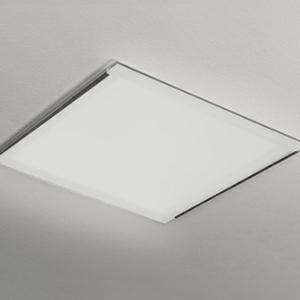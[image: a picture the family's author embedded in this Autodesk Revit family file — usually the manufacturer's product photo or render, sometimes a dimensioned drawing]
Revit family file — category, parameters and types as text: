
# Revit family: 3f_filippi_-_lucequadro_vop_3f_filippi_-_36584_-_lucequadro_led_3000_vop
name_source: partatom
category: Lighting Fixtures
units: mm (PartAtom-declared; Revit-internal decimal feet)

## family parameters
Cut with Voids When Loaded = No
Host = Face
Light Source = No
Part Type = Normal
Room Calculation Point = No
Round Connector Dimension = Use Diameter
Shared = No

## types (1)
- 3F Filippi - Lucequadro VOP (1 x LED, 1929 lm, 28 W, 4000 K)
    Apparent Load = 28 VA
    Approval mark = ENEC
    CIE Flux Codes = 47 79 96 100 100
    Color Rendering = 80
    Color Temperature = 4000 K
    Control Gear = Electronic ballast
    Default Elevation = 1800 mm
    Description = ILLUMINOTECHNICAL
Luminous efficiency 100% (DLOR 100%, ULOR 0%).
Initial luminous flux of the luminaire 1929 lm.
Direct distribution with soft, diffused and controlled light.
Installation Interdistance Transv.D = 1.25 x hu - Long.D = 1.24 x hu.
Tabular UGR (CIE 117 - 4H-8H; S=0.25H; 70/50/20): RUG 24.8 - 24.6.
Beam angle: 113° - 112°.
Luminous efficacy 69 lm/W.
Lifetime (L90/B10): 30000 h. (tq+25°C)
Lifetime (L85/B10): 50000 h. (tq+25°C)
Lifetime (L70/B10): 80000 h. (tq+25°C)
Sudden decreased luminous flux after 50000 hours: 0% (C0).
Photobiological safety in compliance with IEC/TR 62778: RG1 low risk, (IEC 62471).
In compliance with IEC/EN 62722-2-1 - IEC/EN 62717 standards.

SOURCE
Compact LED module 3000/840.
Energy efficiency class (UE 2019/2020 - UE 2019/2015): D.
CIE 13.3 Colour rendering index: CRI >80 (R9 <50%).
IES TM-30 Fidelity Index: Rf = 84 Rg = 95.
CCT nominal colour temperature 4000 K.
Colour initial tolerance (MacAdam): SDCM 3.
Zhaga Book 3 compliant.

MECHANICAL
Housing in white painted steel.
Passive heat dissipator in anodised aluminium, oversized, for optimum thermal management of the LED module.
Flow recuperator in specular aluminium with superficial titanium-magnesium treatment, non-iridescent.
Glazed opal glass, tempered, thickness 4 mm.
Lock-in mounting of the glass in the lateral seats in specular aluminium.
Fixing brackets in galvanised steel.
Slot-cover polycarbonate casings.
Dimensions: 235x235 mm, height 116 mm. Weight 2.15 kg.
IP44 protection degree for exposed part, IP20 for recessed part.
Mechanical strength to impacts IK08 (5 joule).
Glow-wire test resistance 960°C.

ELECTRICAL
Wiring on a separate unit.
Halogen Free electronic wiring 230V-50/60Hz, power factor 0.95, THD <25%, constant output current, SELV, class II, 1 driver.
Power of the luminaire 28 W.
CE - IEC 60598-1 - EN 60598-1.
SAFE FLICKER: PstLM=<1 and SVM=<0.4 (IEC TR 61547-1 and IEC TR 63158), to ensure a more comfortable and safe light.
Ambient temperature from 0°C to +25°C.
Temperature class T6 max 85°C.
Relative humidity UR: <85%.

INSTALLATION
Pull-up recessed fitting.
False ceiling carving: 210x210 mm.
All accessories dedicated to this product are available on the Catalog and on our website www.3F-Filippi.com.

ACCESSORIES
A0189 - Pair of reinforcing brackets for mineral fibre, metal and plasterboard panels, height 20 mm.

APPLICATIONS
Transit areas, corridors, commercial environments, display areas, shops and shop windows.

WARNING
Luminaire designed for disposal/recycling at end-of-life.
Replaceable (LED only) light source by a professional. Replaceable control gear by a professional.
    Height = 0 mm  [stored 0 ft]
    Lamp = 1 x LED
    Lamp Light Flux = 1929 lm
    Lamp Power = 28 W
    Lamp count = 1
    Length = 235 mm
    Lifetime = 50000 h
    Luminous efficacy = 69 lm/W
    Manufacturer = 3F Filippi
    ModVariant = No
    Model = 3F Filippi - 36584 - Lucequadro LED 3000 VOP
    Mounting Place = Ceiling
    Mounting Type = Recessed
    Number of Poles = 1
    OnlyDefault = Yes
    Power Factor = 1
    Product Name = 3F Filippi - Lucequadro VOP
    Product group = recessed luminaire
    ProductGroupID = 4
    Protection Class = Protection class II
    Protection Degree = IP 20
    RLX_Detail_Level = 1
    RLX_Emergency_Light_Flux = 0 lm
    RLX_Emergency_Type = 0
    RLX_Emergency_Type_DB = No
    RlxData = <blob elided: 54069 chars, md5=a92a2420>
    Socket = socket
    Standby Power = 0 W
    System Light Flux = 1929 lm
    System Power = 28 W
    Type Comments = Product without accessories
    Type Image = 3ffilippi_36584.jpg
    URL = http://relux.com
    VarID = ---
    Voltage = 0 V
    Weight = 0.00 kg
    Width = 235 mm

note: [stored X ft] marks values corroborated as IEEE doubles in the binary element streams (Revit-internal decimal feet)

## geometry (parser evidence)
native form markers: Blend x4, Sweep x14
no freeform markers — native parametric forms only
